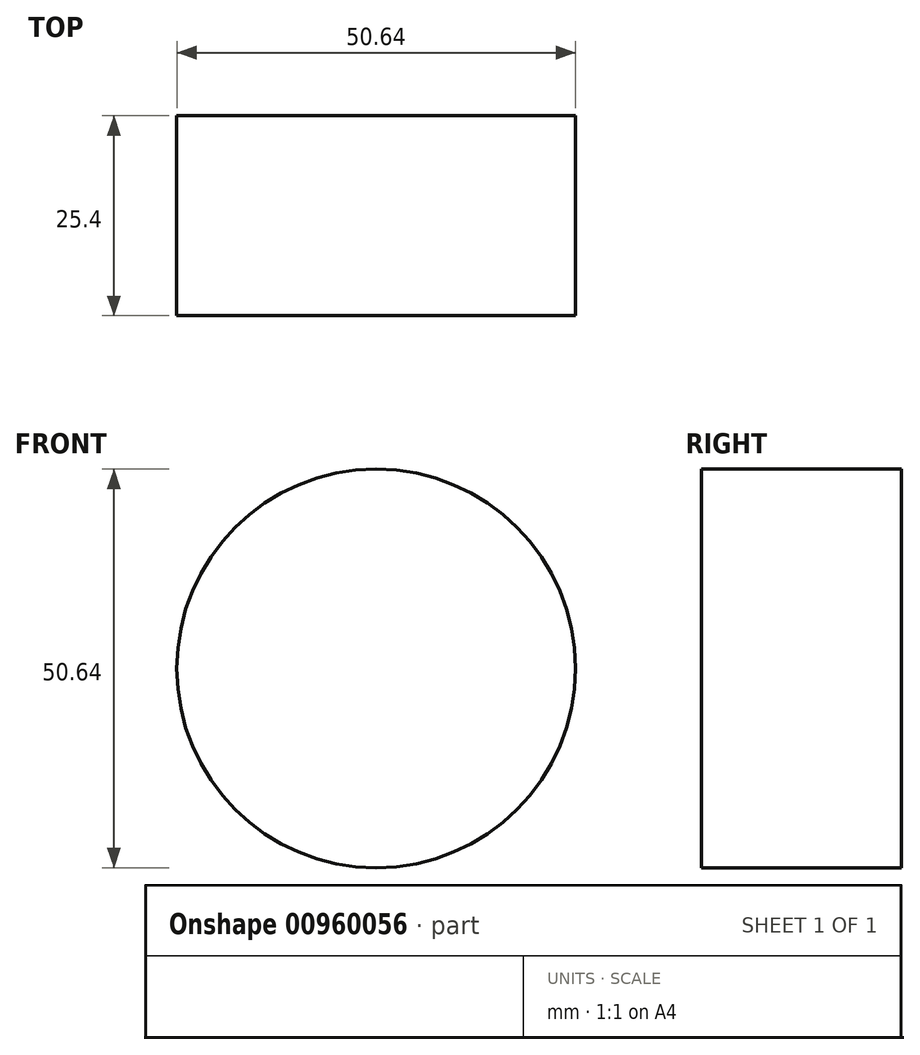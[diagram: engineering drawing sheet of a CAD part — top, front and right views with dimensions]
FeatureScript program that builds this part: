
annotation { "Feature Type Name" : "Feature", "Feature Type Description" : "" }
export const myFeature = defineFeature(function(context is Context, id is Id, definition is map)
    precondition{}
    {
        {
            var Q0;
            Q0=qCreatedBy(makeId("Front.planeOp"),FACE);
            var sketch = newSketch(context, id + "F0", { "sketchPlane" : qUnion([Q0])});
            skCircle(sketch, "E0", {"center": v(0, 0) * mm, "radius": 25.32 * mm});
            skSolve(sketch);
        }
        {
            var Q0;
            Q0 = qSketchRegion(id + "F0", true);
            extrude(context, id + "F1", {"entities" : qUnion([Q0]), "depth" : 25.4 * mm, "offsetDistance" : 25.4 * mm});
        }
    });
